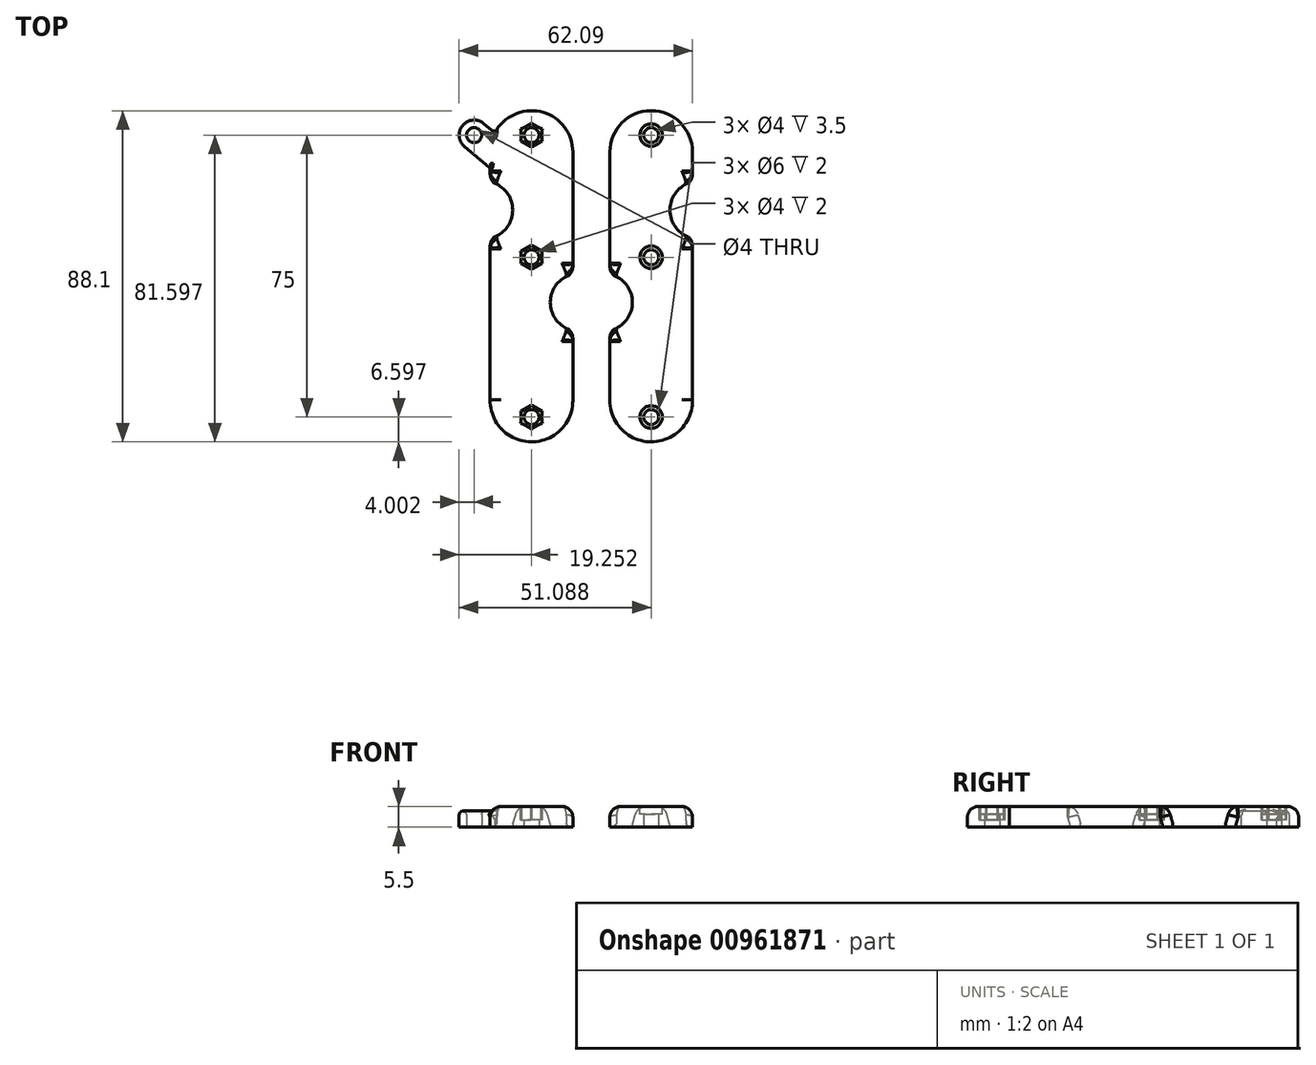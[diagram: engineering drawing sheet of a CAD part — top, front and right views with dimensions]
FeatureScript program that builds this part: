
annotation { "Feature Type Name" : "Feature", "Feature Type Description" : "" }
export const myFeature = defineFeature(function(context is Context, id is Id, definition is map)
    precondition{}
    {
        {
            var Q0;
            Q0=qCreatedBy(makeId("Top.planeOp"),FACE);
            var sketch = newSketch(context, id + "F0", { "sketchPlane" : qUnion([Q0])});
            skCircle(sketch, "E0", {"center": v(-15.92, -0.56) * mm, "radius": 2 * mm});
            skCircle(sketch, "E1", {"center": v(-15.92, 31.94) * mm, "radius": 2 * mm});
            skCircle(sketch, "E2", {"center": v(-15.92, -43.06) * mm, "radius": 2 * mm});
            skLineSegment(sketch, "E3", {"start": v(-26.92, 27.44) * mm, "end": v(-26.92, -38.46) * mm});
            skLineSegment(sketch, "E4", {"start": v(-4.92, 27.44) * mm, "end": v(-4.92, -38.66) * mm});
            skLineSegment(sketch, "E5", {"start": v(-26.92, 27.44) * mm, "end": v(-4.92, 27.44) * mm, "construction": true});
            skPoint(sketch, "E6", {"position": v(-15.92, 27.44) * mm});
            skPoint(sketch, "E7", {"position": v(-17.92, 31.94) * mm});
            skPoint(sketch, "E8", {"position": v(-13.92, 31.94) * mm});
            skLineSegment(sketch, "E9", {"start": v(-26.92, -38.46) * mm, "end": v(-4.92, -38.66) * mm, "construction": true});
            skPoint(sketch, "E10", {"position": v(-15.92, -38.56) * mm});
            skArc(sketch, "E11", {"start": v(-4.92, 27.44) * mm, "mid": v(-15.92, 38.44) * mm, "end": v(-26.92, 27.44) * mm});
            skArc(sketch, "E12", {"start": v(-26.92, -38.46) * mm, "mid": v(-16.02, -49.66) * mm, "end": v(-4.92, -38.66) * mm});
            skPoint(sketch, "E13", {"position": v(-26.92, 12) * mm});
            skPoint(sketch, "E14", {"position": v(-4.92, -12.56) * mm});
            skPoint(sketch, "E15", {"position": v(-26.92, 0) * mm});
            skPoint(sketch, "E16", {"position": v(-4.92, -0.56) * mm});
            skArc(sketch, "E17", {"start": v(-26.92, 4.5) * mm, "mid": v(-20.92, 12) * mm, "end": v(-26.92, 19.5) * mm});
            skArc(sketch, "E18", {"start": v(-4.92, -5.06) * mm, "mid": v(-10.92, -12.56) * mm, "end": v(-4.92, -20.06) * mm});
            skSolve(sketch);
        }
        {
            var Q0;
            Q0=makeQuery(id+"F0.imprint","IMPRINT",FACE,{"disambiguationData":[TD([[makeQuery(id+"F0.imprint","IMPRINT",EDGE,{"derivedFrom":sQuery(id+"F0.wireOp",EDGE,"E0")}),-1.0]])]});
            extrude(context, id + "F1", {"entities" : qUnion([Q0]), "depth" : 5.5 * mm, "offsetDistance" : 25 * mm});
        }
        {
            var Q0;
            Q0=makeQuery(id+"F1.opExtrude","CAP_EDGE",EDGE,{"disambiguationData":[OSD([sQuery(id+"F0.wireOp",EDGE,"E17")])],"isStart":false});
            var Q1;
            Q1=makeQuery(id+"F1.opExtrude","CAP_EDGE",EDGE,{"disambiguationData":[OSD([sQuery(id+"F0.wireOp",EDGE,"E18")])],"isStart":false});
            chamfer(context, id + "F2", {"entities" : qUnion([Q0, Q1]), "chamferType" : ChamferType.OFFSET_ANGLE, "width" : 5 * mm, "oppositeDirection" : false, "angle" : 15 * degree, "tangentPropagation" : true});
        }
        {
            var Q0;
            {var subQ0=sQuery(id+"F0.wireOp",EDGE,"E3");Q0=makeQuery(id+"F1.opExtrude","CAP_EDGE",EDGE,{"disambiguationData":[OSD([subQ0]),TDD([makeQuery(id+"F0.imprint","IMPRINT",EDGE,{"disambiguationData":[TD([[makeQuery(id+"F0.imprint","INTERSECT",VERTEX,{"derivedFrom":[subQ0,sQuery(id+"F0.wireOp",EDGE,"E12")]}),1.0]])],"derivedFrom":subQ0})])],"isStart":false});}
            var Q1;
            Q1=makeQuery(id+"F1.opExtrude","CAP_EDGE",EDGE,{"disambiguationData":[OSD([sQuery(id+"F0.wireOp",EDGE,"E11")])],"isStart":false});
            var Q2;
            Q2=makeQuery(id+"F1.opExtrude","CAP_EDGE",EDGE,{"disambiguationData":[OSD([sQuery(id+"F0.wireOp",EDGE,"E12")])],"isStart":false});
            fillet(context, id + "F3", {"entities" : qUnion([Q0, Q1, Q2]), "radius" : 2.85 * mm, "tangentPropagation" : true, "allowEdgeOverflow" : false});
        }
        {
            var Q0;
            {var subQ0=sQuery(id+"F0.wireOp",EDGE,"E17");Q0=makeQuery(id+"F2.opChamfer","BLEND_EDGE",EDGE,{"blendedFrom":[makeQuery(id+"F1.opExtrude","CAP_EDGE",EDGE,{"disambiguationData":[OSD([subQ0])],"isStart":false}),makeQuery(id+"F1.opExtrude","SWEPT_FACE",FACE,{"disambiguationData":[OSD([subQ0])]})],"blendedInto":[makeQuery(id+"F1.opExtrude","SWEPT_FACE",FACE,{"disambiguationData":[OSD([subQ0])]})]});}
            var Q1;
            {var subQ0=sQuery(id+"F0.wireOp",EDGE,"E18");Q1=makeQuery(id+"F2.opChamfer","BLEND_EDGE",EDGE,{"blendedFrom":[makeQuery(id+"F1.opExtrude","CAP_EDGE",EDGE,{"disambiguationData":[OSD([subQ0])],"isStart":false}),makeQuery(id+"F1.opExtrude","SWEPT_FACE",FACE,{"disambiguationData":[OSD([subQ0])]})],"blendedInto":[makeQuery(id+"F1.opExtrude","SWEPT_FACE",FACE,{"disambiguationData":[OSD([subQ0])]})]});}
            var Q2;
            {var subQ0=sQuery(id+"F0.wireOp",EDGE,"E17");Q2=makeQuery(id+"F2.opChamfer","BLEND_EDGE",EDGE,{"blendedFrom":[makeQuery(id+"F1.opExtrude","CAP_EDGE",EDGE,{"disambiguationData":[OSD([subQ0])],"isStart":false}),makeQuery(id+"F1.opExtrude","CAP_FACE",FACE,{"disambiguationData":[OSD([sQuery(id+"F0.wireOp",EDGE,"E0"),sQuery(id+"F0.wireOp",EDGE,"E1"),sQuery(id+"F0.wireOp",EDGE,"E2"),sQuery(id+"F0.wireOp",EDGE,"E3"),sQuery(id+"F0.wireOp",EDGE,"E4"),sQuery(id+"F0.wireOp",EDGE,"E11"),sQuery(id+"F0.wireOp",EDGE,"E12"),subQ0,sQuery(id+"F0.wireOp",EDGE,"E18")])],"isStart":false})],"blendedInto":[makeQuery(id+"F1.opExtrude","CAP_FACE",FACE,{"disambiguationData":[OSD([sQuery(id+"F0.wireOp",EDGE,"E0"),sQuery(id+"F0.wireOp",EDGE,"E1"),sQuery(id+"F0.wireOp",EDGE,"E2"),sQuery(id+"F0.wireOp",EDGE,"E3"),sQuery(id+"F0.wireOp",EDGE,"E4"),sQuery(id+"F0.wireOp",EDGE,"E11"),sQuery(id+"F0.wireOp",EDGE,"E12"),subQ0,sQuery(id+"F0.wireOp",EDGE,"E18")])],"isStart":false})]});}
            var Q3;
            {var subQ0=sQuery(id+"F0.wireOp",EDGE,"E18");Q3=makeQuery(id+"F2.opChamfer","BLEND_EDGE",EDGE,{"blendedFrom":[makeQuery(id+"F1.opExtrude","CAP_EDGE",EDGE,{"disambiguationData":[OSD([subQ0])],"isStart":false}),makeQuery(id+"F1.opExtrude","CAP_FACE",FACE,{"disambiguationData":[OSD([sQuery(id+"F0.wireOp",EDGE,"E0"),sQuery(id+"F0.wireOp",EDGE,"E1"),sQuery(id+"F0.wireOp",EDGE,"E2"),sQuery(id+"F0.wireOp",EDGE,"E3"),sQuery(id+"F0.wireOp",EDGE,"E4"),sQuery(id+"F0.wireOp",EDGE,"E11"),sQuery(id+"F0.wireOp",EDGE,"E12"),sQuery(id+"F0.wireOp",EDGE,"E17"),subQ0])],"isStart":false})],"blendedInto":[makeQuery(id+"F1.opExtrude","CAP_FACE",FACE,{"disambiguationData":[OSD([sQuery(id+"F0.wireOp",EDGE,"E0"),sQuery(id+"F0.wireOp",EDGE,"E1"),sQuery(id+"F0.wireOp",EDGE,"E2"),sQuery(id+"F0.wireOp",EDGE,"E3"),sQuery(id+"F0.wireOp",EDGE,"E4"),sQuery(id+"F0.wireOp",EDGE,"E11"),sQuery(id+"F0.wireOp",EDGE,"E12"),sQuery(id+"F0.wireOp",EDGE,"E17"),subQ0])],"isStart":false})]});}
            fillet(context, id + "F4", {"entities" : qUnion([Q0, Q1, Q2, Q3]), "radius" : 3 * mm, "tangentPropagation" : true, "allowEdgeOverflow" : false});
        }
        {
            var Q0;
            Q0=makeQuery(id+"F1.opExtrude","SWEPT_BODY",BODY,{"disambiguationData":[OSD([sQuery(id+"F0.wireOp",EDGE,"E0"),sQuery(id+"F0.wireOp",EDGE,"E1"),sQuery(id+"F0.wireOp",EDGE,"E2"),sQuery(id+"F0.wireOp",EDGE,"E3"),sQuery(id+"F0.wireOp",EDGE,"E4"),sQuery(id+"F0.wireOp",EDGE,"E11"),sQuery(id+"F0.wireOp",EDGE,"E12"),sQuery(id+"F0.wireOp",EDGE,"E17"),sQuery(id+"F0.wireOp",EDGE,"E18")])]});
            var Q1;
            Q1=qCreatedBy(makeId("Right.planeOp"),FACE);
            mirror(context, id + "F5", {"entities" : qUnion([Q0]), "mirrorPlane" : qUnion([Q1])});
        }
        {
            var Q0;
            Q0=makeQuery(id+"F5.opPattern","COPY",FACE,{"derivedFrom":makeQuery(id+"F1.opExtrude","CAP_FACE",FACE,{"disambiguationData":[OSD([sQuery(id+"F0.wireOp",EDGE,"E0"),sQuery(id+"F0.wireOp",EDGE,"E1"),sQuery(id+"F0.wireOp",EDGE,"E2"),sQuery(id+"F0.wireOp",EDGE,"E3"),sQuery(id+"F0.wireOp",EDGE,"E4"),sQuery(id+"F0.wireOp",EDGE,"E11"),sQuery(id+"F0.wireOp",EDGE,"E12"),sQuery(id+"F0.wireOp",EDGE,"E17"),sQuery(id+"F0.wireOp",EDGE,"E18")])],"isStart":false}),"instanceName":"1"});
            var sketch = newSketch(context, id + "F6", { "sketchPlane" : qUnion([Q0])});
            skCircle(sketch, "E19", {"center": v(15.92, -0.56) * mm, "radius": 3 * mm});
            skCircle(sketch, "E20", {"center": v(15.92, -43.06) * mm, "radius": 3 * mm});
            skCircle(sketch, "E21", {"center": v(15.92, 31.94) * mm, "radius": 3 * mm});
            skSolve(sketch);
        }
        {
            var Q0;
            Q0=makeQuery(id+"F6.imprint","IMPRINT",FACE,{"disambiguationData":[TD([[makeQuery(id+"F6.imprint","IMPRINT",EDGE,{"derivedFrom":sQuery(id+"F6.wireOp",EDGE,"E21")}),1.0]])]});
            var Q1;
            Q1=makeQuery(id+"F6.imprint","IMPRINT",FACE,{"disambiguationData":[TD([[makeQuery(id+"F6.imprint","IMPRINT",EDGE,{"derivedFrom":sQuery(id+"F6.wireOp",EDGE,"E19")}),1.0]])]});
            var Q2;
            Q2=makeQuery(id+"F6.imprint","IMPRINT",FACE,{"disambiguationData":[TD([[makeQuery(id+"F6.imprint","IMPRINT",EDGE,{"derivedFrom":sQuery(id+"F6.wireOp",EDGE,"E20")}),1.0]])]});
            extrude(context, id + "F7", {"entities" : qUnion([Q0, Q1, Q2]), "operationType" : NewBodyOperationType.REMOVE, "oppositeDirection" : true, "depth" : 2 * mm, "offsetDistance" : 25 * mm});
        }
        {
            var Q0;
            Q0=makeQuery(id+"F1.opExtrude","CAP_FACE",FACE,{"disambiguationData":[OSD([sQuery(id+"F0.wireOp",EDGE,"E0"),sQuery(id+"F0.wireOp",EDGE,"E1"),sQuery(id+"F0.wireOp",EDGE,"E2"),sQuery(id+"F0.wireOp",EDGE,"E3"),sQuery(id+"F0.wireOp",EDGE,"E4"),sQuery(id+"F0.wireOp",EDGE,"E11"),sQuery(id+"F0.wireOp",EDGE,"E12"),sQuery(id+"F0.wireOp",EDGE,"E17"),sQuery(id+"F0.wireOp",EDGE,"E18")])],"isStart":false});
            var sketch = newSketch(context, id + "F8", { "sketchPlane" : qUnion([Q0])});
            skCircle(sketch, "E22.cCircle", {"center": v(-15.92, -0.56) * mm, "radius": 2.75 * mm, "construction": true});
            skLineSegment(sketch, "E22.0", {"start": v(-15.92, 2.61) * mm, "end": v(-13.17, 1.03) * mm});
            skLineSegment(sketch, "E22.1", {"start": v(-13.17, 1.03) * mm, "end": v(-13.17, -2.15) * mm});
            skLineSegment(sketch, "E22.2", {"start": v(-13.17, -2.15) * mm, "end": v(-15.92, -3.74) * mm});
            skLineSegment(sketch, "E22.3", {"start": v(-15.92, -3.74) * mm, "end": v(-18.67, -2.15) * mm});
            skLineSegment(sketch, "E22.4", {"start": v(-18.67, -2.15) * mm, "end": v(-18.67, 1.03) * mm});
            skLineSegment(sketch, "E22.5", {"start": v(-18.67, 1.03) * mm, "end": v(-15.92, 2.61) * mm});
            skPoint(sketch, "E22.0.midPoint", {"position": v(-14.54, 1.82) * mm});
            skCircle(sketch, "E23.cCircle", {"center": v(-15.92, 31.94) * mm, "radius": 2.75 * mm, "construction": true});
            skLineSegment(sketch, "E23.0", {"start": v(-13.17, 30.35) * mm, "end": v(-15.92, 28.76) * mm});
            skLineSegment(sketch, "E23.1", {"start": v(-15.92, 28.76) * mm, "end": v(-18.67, 30.35) * mm});
            skLineSegment(sketch, "E23.2", {"start": v(-18.67, 30.35) * mm, "end": v(-18.67, 33.53) * mm});
            skLineSegment(sketch, "E23.3", {"start": v(-18.67, 33.53) * mm, "end": v(-15.92, 35.11) * mm});
            skLineSegment(sketch, "E23.4", {"start": v(-15.92, 35.11) * mm, "end": v(-13.17, 33.53) * mm});
            skLineSegment(sketch, "E23.5", {"start": v(-13.17, 33.53) * mm, "end": v(-13.17, 30.35) * mm});
            skPoint(sketch, "E23.0.midPoint", {"position": v(-14.54, 29.56) * mm});
            skCircle(sketch, "E24.cCircle", {"center": v(-15.92, -43.06) * mm, "radius": 2.75 * mm, "construction": true});
            skLineSegment(sketch, "E24.0", {"start": v(-15.92, -39.89) * mm, "end": v(-13.17, -41.47) * mm});
            skLineSegment(sketch, "E24.1", {"start": v(-13.17, -41.47) * mm, "end": v(-13.17, -44.65) * mm});
            skLineSegment(sketch, "E24.2", {"start": v(-13.17, -44.65) * mm, "end": v(-15.92, -46.24) * mm});
            skLineSegment(sketch, "E24.3", {"start": v(-15.92, -46.24) * mm, "end": v(-18.67, -44.65) * mm});
            skLineSegment(sketch, "E24.4", {"start": v(-18.67, -44.65) * mm, "end": v(-18.67, -41.47) * mm});
            skLineSegment(sketch, "E24.5", {"start": v(-18.67, -41.47) * mm, "end": v(-15.92, -39.89) * mm});
            skPoint(sketch, "E24.0.midPoint", {"position": v(-14.54, -40.68) * mm});
            skCircle(sketch, "E25.cCircle", {"center": v(-15.92, -0.56) * mm, "radius": 1.69 * mm, "construction": true});
            skLineSegment(sketch, "E25.0", {"start": v(-13, -2.25) * mm, "end": v(-15.92, 2.81) * mm});
            skLineSegment(sketch, "E25.1", {"start": v(-13, -2.25) * mm, "end": v(-18.84, -2.25) * mm});
            skLineSegment(sketch, "E25.2", {"start": v(-15.92, 2.81) * mm, "end": v(-18.84, -2.25) * mm});
            skPoint(sketch, "E25.0.midPoint", {"position": v(-14.46, 0.28) * mm});
            skLineSegment(sketch, "E26.0", {"start": v(-13, 1.13) * mm, "end": v(-15.92, -3.94) * mm});
            skLineSegment(sketch, "E26.1", {"start": v(-15.92, -3.94) * mm, "end": v(-18.84, 1.13) * mm});
            skLineSegment(sketch, "E26.2", {"start": v(-18.84, 1.13) * mm, "end": v(-13, 1.13) * mm});
            skPoint(sketch, "E26.0.midPoint", {"position": v(-14.46, -1.4) * mm});
            skCircle(sketch, "E27.cCircle", {"center": v(-15.92, 31.94) * mm, "radius": 1.69 * mm, "construction": true});
            skLineSegment(sketch, "E27.0", {"start": v(-18.84, 33.63) * mm, "end": v(-13, 33.63) * mm});
            skLineSegment(sketch, "E27.1", {"start": v(-13, 33.63) * mm, "end": v(-15.92, 28.56) * mm});
            skLineSegment(sketch, "E27.2", {"start": v(-15.92, 28.56) * mm, "end": v(-18.84, 33.63) * mm});
            skPoint(sketch, "E27.0.midPoint", {"position": v(-15.92, 33.63) * mm});
            skLineSegment(sketch, "E28.0", {"start": v(-13, 30.25) * mm, "end": v(-18.84, 30.25) * mm});
            skLineSegment(sketch, "E28.1", {"start": v(-18.84, 30.25) * mm, "end": v(-15.92, 35.31) * mm});
            skLineSegment(sketch, "E28.2", {"start": v(-15.92, 35.31) * mm, "end": v(-13, 30.25) * mm});
            skPoint(sketch, "E28.0.midPoint", {"position": v(-15.92, 30.25) * mm});
            skCircle(sketch, "E29.cCircle", {"center": v(-15.92, -43.06) * mm, "radius": 1.69 * mm, "construction": true});
            skLineSegment(sketch, "E29.0", {"start": v(-18.84, -41.37) * mm, "end": v(-13, -41.37) * mm});
            skLineSegment(sketch, "E29.1", {"start": v(-13, -41.37) * mm, "end": v(-15.92, -46.44) * mm});
            skLineSegment(sketch, "E29.2", {"start": v(-15.92, -46.44) * mm, "end": v(-18.84, -41.37) * mm});
            skPoint(sketch, "E29.0.midPoint", {"position": v(-15.92, -41.37) * mm});
            skLineSegment(sketch, "E30.0", {"start": v(-13, -44.75) * mm, "end": v(-18.84, -44.75) * mm});
            skLineSegment(sketch, "E30.1", {"start": v(-18.84, -44.75) * mm, "end": v(-15.92, -39.69) * mm});
            skLineSegment(sketch, "E30.2", {"start": v(-15.92, -39.69) * mm, "end": v(-13, -44.75) * mm});
            skPoint(sketch, "E30.0.midPoint", {"position": v(-15.92, -44.75) * mm});
            skSolve(sketch);
        }
        {
            var Q0;
            {var subQ0=sQuery(id+"F8.wireOp",EDGE,"E22.5");var subQ1=sQuery(id+"F8.wireOp",EDGE,"E22.4");var subQ2=makeQuery(id+"F8.imprint","INTERSECT",VERTEX,{"derivedFrom":[subQ1,subQ0]});Q0=makeQuery(id+"F8.imprint","IMPRINT",FACE,{"disambiguationData":[TD([[makeQuery(id+"F8.imprint","IMPRINT",EDGE,{"disambiguationData":[TD([[subQ2,1.0]])],"derivedFrom":subQ1}),1.0]])]});}
            var Q1;
            {var subQ1=sQuery(id+"F8.wireOp",EDGE,"E22.5");var subQ6=sQuery(id+"F8.wireOp",EDGE,"E22.4");var subQ9=makeQuery(id+"F8.imprint","INTERSECT",VERTEX,{"derivedFrom":[subQ6,subQ1]});Q1=makeQuery(id+"F8.imprint","IMPRINT",FACE,{"disambiguationData":[TD([[makeQuery(id+"F8.imprint","IMPRINT",EDGE,{"disambiguationData":[TD([[subQ9,1.0]])],"derivedFrom":subQ6}),-1.0]])]});}
            var Q2;
            {var subQ0=sQuery(id+"F8.wireOp",EDGE,"E26.2");var subQ1=sQuery(id+"F8.wireOp",EDGE,"E22.5");var subQ2=makeQuery(id+"F8.imprint","INTERSECT",VERTEX,{"derivedFrom":[subQ1,subQ0]});Q2=makeQuery(id+"F8.imprint","IMPRINT",FACE,{"disambiguationData":[TD([[makeQuery(id+"F8.imprint","IMPRINT",EDGE,{"disambiguationData":[TD([[subQ2,-1.0]])],"derivedFrom":subQ1}),-1.0]])]});}
            var Q3;
            {var subQ0=sQuery(id+"F8.wireOp",EDGE,"E25.2");var subQ1=sQuery(id+"F8.wireOp",EDGE,"E22.4");var subQ2=makeQuery(id+"F8.imprint","INTERSECT",VERTEX,{"derivedFrom":[subQ1,subQ0]});Q3=makeQuery(id+"F8.imprint","IMPRINT",FACE,{"disambiguationData":[TD([[makeQuery(id+"F8.imprint","IMPRINT",EDGE,{"disambiguationData":[TD([[subQ2,-1.0]])],"derivedFrom":subQ1}),-1.0]])]});}
            var Q4;
            {var subQ0=sQuery(id+"F8.wireOp",EDGE,"E22.4");var subQ1=sQuery(id+"F8.wireOp",EDGE,"E22.3");var subQ2=makeQuery(id+"F8.imprint","INTERSECT",VERTEX,{"derivedFrom":[subQ1,subQ0]});Q4=makeQuery(id+"F8.imprint","IMPRINT",FACE,{"disambiguationData":[TD([[makeQuery(id+"F8.imprint","IMPRINT",EDGE,{"disambiguationData":[TD([[subQ2,1.0]])],"derivedFrom":subQ1}),1.0]])]});}
            var Q5;
            {var subQ1=sQuery(id+"F8.wireOp",EDGE,"E22.4");var subQ6=sQuery(id+"F8.wireOp",EDGE,"E22.3");var subQ9=makeQuery(id+"F8.imprint","INTERSECT",VERTEX,{"derivedFrom":[subQ6,subQ1]});Q5=makeQuery(id+"F8.imprint","IMPRINT",FACE,{"disambiguationData":[TD([[makeQuery(id+"F8.imprint","IMPRINT",EDGE,{"disambiguationData":[TD([[subQ9,1.0]])],"derivedFrom":subQ6}),-1.0]])]});}
            var Q6;
            {var subQ0=sQuery(id+"F8.wireOp",EDGE,"E26.1");var subQ1=sQuery(id+"F8.wireOp",EDGE,"E22.3");var subQ2=makeQuery(id+"F8.imprint","INTERSECT",VERTEX,{"derivedFrom":[subQ1,subQ0]});Q6=makeQuery(id+"F8.imprint","IMPRINT",FACE,{"disambiguationData":[TD([[makeQuery(id+"F8.imprint","IMPRINT",EDGE,{"disambiguationData":[TD([[subQ2,-1.0]])],"derivedFrom":subQ1}),-1.0]])]});}
            var Q7;
            {var subQ1=sQuery(id+"F8.wireOp",EDGE,"E22.2");var subQ6=sQuery(id+"F8.wireOp",EDGE,"E22.3");var subQ9=makeQuery(id+"F8.imprint","INTERSECT",VERTEX,{"derivedFrom":[subQ1,subQ6]});Q7=makeQuery(id+"F8.imprint","IMPRINT",FACE,{"disambiguationData":[TD([[makeQuery(id+"F8.imprint","IMPRINT",EDGE,{"disambiguationData":[TD([[subQ9,1.0]])],"derivedFrom":subQ1}),-1.0]])]});}
            var Q8;
            {var subQ0=sQuery(id+"F8.wireOp",EDGE,"E25.1");var subQ1=sQuery(id+"F8.wireOp",EDGE,"E22.2");var subQ2=makeQuery(id+"F8.imprint","INTERSECT",VERTEX,{"derivedFrom":[subQ1,subQ0]});Q8=makeQuery(id+"F8.imprint","IMPRINT",FACE,{"disambiguationData":[TD([[makeQuery(id+"F8.imprint","IMPRINT",EDGE,{"disambiguationData":[TD([[subQ2,-1.0]])],"derivedFrom":subQ1}),-1.0]])]});}
            var Q9;
            {var subQ1=sQuery(id+"F8.wireOp",EDGE,"E22.2");var subQ5=sQuery(id+"F8.wireOp",EDGE,"E22.1");var subQ6=makeQuery(id+"F8.imprint","INTERSECT",VERTEX,{"derivedFrom":[subQ5,subQ1]});Q9=makeQuery(id+"F8.imprint","IMPRINT",FACE,{"disambiguationData":[TD([[makeQuery(id+"F8.imprint","IMPRINT",EDGE,{"disambiguationData":[TD([[subQ6,1.0]])],"derivedFrom":subQ5}),-1.0]])]});}
            var Q10;
            {var subQ0=sQuery(id+"F8.wireOp",EDGE,"E26.0");var subQ1=sQuery(id+"F8.wireOp",EDGE,"E22.1");var subQ2=makeQuery(id+"F8.imprint","INTERSECT",VERTEX,{"derivedFrom":[subQ1,subQ0]});Q10=makeQuery(id+"F8.imprint","IMPRINT",FACE,{"disambiguationData":[TD([[makeQuery(id+"F8.imprint","IMPRINT",EDGE,{"disambiguationData":[TD([[subQ2,-1.0]])],"derivedFrom":subQ1}),-1.0]])]});}
            var Q11;
            {var subQ1=sQuery(id+"F8.wireOp",EDGE,"E22.0");var subQ5=sQuery(id+"F8.wireOp",EDGE,"E22.1");var subQ6=makeQuery(id+"F8.imprint","INTERSECT",VERTEX,{"derivedFrom":[subQ1,subQ5]});Q11=makeQuery(id+"F8.imprint","IMPRINT",FACE,{"disambiguationData":[TD([[makeQuery(id+"F8.imprint","IMPRINT",EDGE,{"disambiguationData":[TD([[subQ6,1.0]])],"derivedFrom":subQ1}),-1.0]])]});}
            var Q12;
            {var subQ0=sQuery(id+"F8.wireOp",EDGE,"E25.0");var subQ1=sQuery(id+"F8.wireOp",EDGE,"E22.0");var subQ2=makeQuery(id+"F8.imprint","INTERSECT",VERTEX,{"derivedFrom":[subQ1,subQ0]});Q12=makeQuery(id+"F8.imprint","IMPRINT",FACE,{"disambiguationData":[TD([[makeQuery(id+"F8.imprint","IMPRINT",EDGE,{"disambiguationData":[TD([[subQ2,-1.0]])],"derivedFrom":subQ1}),-1.0]])]});}
            var Q13;
            {var subQ0=sQuery(id+"F8.wireOp",EDGE,"E22.5");var subQ1=sQuery(id+"F8.wireOp",EDGE,"E22.0");var subQ2=makeQuery(id+"F8.imprint","INTERSECT",VERTEX,{"derivedFrom":[subQ1,subQ0]});Q13=makeQuery(id+"F8.imprint","IMPRINT",FACE,{"disambiguationData":[TD([[makeQuery(id+"F8.imprint","IMPRINT",EDGE,{"disambiguationData":[TD([[subQ2,-1.0]])],"derivedFrom":subQ1}),-1.0]])]});}
            var Q14;
            {var subQ0=sQuery(id+"F8.wireOp",EDGE,"E22.3");var subQ1=sQuery(id+"F8.wireOp",EDGE,"E22.2");var subQ2=makeQuery(id+"F8.imprint","INTERSECT",VERTEX,{"derivedFrom":[subQ1,subQ0]});Q14=makeQuery(id+"F8.imprint","IMPRINT",FACE,{"disambiguationData":[TD([[makeQuery(id+"F8.imprint","IMPRINT",EDGE,{"disambiguationData":[TD([[subQ2,1.0]])],"derivedFrom":subQ1}),1.0]])]});}
            var Q15;
            {var subQ0=sQuery(id+"F8.wireOp",EDGE,"E22.2");var subQ1=sQuery(id+"F8.wireOp",EDGE,"E22.1");var subQ2=makeQuery(id+"F8.imprint","INTERSECT",VERTEX,{"derivedFrom":[subQ1,subQ0]});Q15=makeQuery(id+"F8.imprint","IMPRINT",FACE,{"disambiguationData":[TD([[makeQuery(id+"F8.imprint","IMPRINT",EDGE,{"disambiguationData":[TD([[subQ2,1.0]])],"derivedFrom":subQ1}),1.0]])]});}
            var Q16;
            {var subQ0=sQuery(id+"F8.wireOp",EDGE,"E22.1");var subQ1=sQuery(id+"F8.wireOp",EDGE,"E22.0");var subQ2=makeQuery(id+"F8.imprint","INTERSECT",VERTEX,{"derivedFrom":[subQ1,subQ0]});Q16=makeQuery(id+"F8.imprint","IMPRINT",FACE,{"disambiguationData":[TD([[makeQuery(id+"F8.imprint","IMPRINT",EDGE,{"disambiguationData":[TD([[subQ2,1.0]])],"derivedFrom":subQ1}),1.0]])]});}
            var Q17;
            {var subQ0=sQuery(id+"F8.wireOp",EDGE,"E22.5");var subQ1=sQuery(id+"F8.wireOp",EDGE,"E22.0");var subQ2=makeQuery(id+"F8.imprint","INTERSECT",VERTEX,{"derivedFrom":[subQ1,subQ0]});Q17=makeQuery(id+"F8.imprint","IMPRINT",FACE,{"disambiguationData":[TD([[makeQuery(id+"F8.imprint","IMPRINT",EDGE,{"disambiguationData":[TD([[subQ2,-1.0]])],"derivedFrom":subQ1}),1.0]])]});}
            var Q18;
            {var subQ0=sQuery(id+"F8.wireOp",EDGE,"E27.2");var subQ1=sQuery(id+"F8.wireOp",EDGE,"E23.1");var subQ2=makeQuery(id+"F8.imprint","INTERSECT",VERTEX,{"derivedFrom":[subQ1,subQ0]});Q18=makeQuery(id+"F8.imprint","IMPRINT",FACE,{"disambiguationData":[TD([[makeQuery(id+"F8.imprint","IMPRINT",EDGE,{"disambiguationData":[TD([[subQ2,-1.0]])],"derivedFrom":subQ1}),-1.0]])]});}
            var Q19;
            {var subQ1=sQuery(id+"F8.wireOp",EDGE,"E23.1");var subQ6=sQuery(id+"F8.wireOp",EDGE,"E23.0");var subQ9=makeQuery(id+"F8.imprint","INTERSECT",VERTEX,{"derivedFrom":[subQ6,subQ1]});Q19=makeQuery(id+"F8.imprint","IMPRINT",FACE,{"disambiguationData":[TD([[makeQuery(id+"F8.imprint","IMPRINT",EDGE,{"disambiguationData":[TD([[subQ9,1.0]])],"derivedFrom":subQ6}),-1.0]])]});}
            var Q20;
            {var subQ0=sQuery(id+"F8.wireOp",EDGE,"E28.0");var subQ1=sQuery(id+"F8.wireOp",EDGE,"E23.0");var subQ2=makeQuery(id+"F8.imprint","INTERSECT",VERTEX,{"derivedFrom":[subQ1,subQ0]});Q20=makeQuery(id+"F8.imprint","IMPRINT",FACE,{"disambiguationData":[TD([[makeQuery(id+"F8.imprint","IMPRINT",EDGE,{"disambiguationData":[TD([[subQ2,-1.0]])],"derivedFrom":subQ1}),-1.0]])]});}
            var Q21;
            {var subQ1=sQuery(id+"F8.wireOp",EDGE,"E23.5");var subQ6=sQuery(id+"F8.wireOp",EDGE,"E23.0");var subQ9=makeQuery(id+"F8.imprint","INTERSECT",VERTEX,{"derivedFrom":[subQ6,subQ1]});Q21=makeQuery(id+"F8.imprint","IMPRINT",FACE,{"disambiguationData":[TD([[makeQuery(id+"F8.imprint","IMPRINT",EDGE,{"disambiguationData":[TD([[subQ9,-1.0]])],"derivedFrom":subQ6}),-1.0]])]});}
            var Q22;
            {var subQ0=sQuery(id+"F8.wireOp",EDGE,"E27.1");var subQ1=sQuery(id+"F8.wireOp",EDGE,"E23.5");var subQ2=makeQuery(id+"F8.imprint","INTERSECT",VERTEX,{"derivedFrom":[subQ1,subQ0]});Q22=makeQuery(id+"F8.imprint","IMPRINT",FACE,{"disambiguationData":[TD([[makeQuery(id+"F8.imprint","IMPRINT",EDGE,{"disambiguationData":[TD([[subQ2,-1.0]])],"derivedFrom":subQ1}),-1.0]])]});}
            var Q23;
            {var subQ1=sQuery(id+"F8.wireOp",EDGE,"E23.4");var subQ5=sQuery(id+"F8.wireOp",EDGE,"E23.5");var subQ6=makeQuery(id+"F8.imprint","INTERSECT",VERTEX,{"derivedFrom":[subQ1,subQ5]});Q23=makeQuery(id+"F8.imprint","IMPRINT",FACE,{"disambiguationData":[TD([[makeQuery(id+"F8.imprint","IMPRINT",EDGE,{"disambiguationData":[TD([[subQ6,1.0]])],"derivedFrom":subQ1}),-1.0]])]});}
            var Q24;
            {var subQ0=sQuery(id+"F8.wireOp",EDGE,"E28.2");var subQ1=sQuery(id+"F8.wireOp",EDGE,"E23.4");var subQ2=makeQuery(id+"F8.imprint","INTERSECT",VERTEX,{"derivedFrom":[subQ1,subQ0]});Q24=makeQuery(id+"F8.imprint","IMPRINT",FACE,{"disambiguationData":[TD([[makeQuery(id+"F8.imprint","IMPRINT",EDGE,{"disambiguationData":[TD([[subQ2,-1.0]])],"derivedFrom":subQ1}),-1.0]])]});}
            var Q25;
            {var subQ1=sQuery(id+"F8.wireOp",EDGE,"E23.3");var subQ5=sQuery(id+"F8.wireOp",EDGE,"E23.4");var subQ6=makeQuery(id+"F8.imprint","INTERSECT",VERTEX,{"derivedFrom":[subQ1,subQ5]});Q25=makeQuery(id+"F8.imprint","IMPRINT",FACE,{"disambiguationData":[TD([[makeQuery(id+"F8.imprint","IMPRINT",EDGE,{"disambiguationData":[TD([[subQ6,1.0]])],"derivedFrom":subQ1}),-1.0]])]});}
            var Q26;
            {var subQ0=sQuery(id+"F8.wireOp",EDGE,"E27.0");var subQ1=sQuery(id+"F8.wireOp",EDGE,"E23.3");var subQ2=makeQuery(id+"F8.imprint","INTERSECT",VERTEX,{"derivedFrom":[subQ1,subQ0]});Q26=makeQuery(id+"F8.imprint","IMPRINT",FACE,{"disambiguationData":[TD([[makeQuery(id+"F8.imprint","IMPRINT",EDGE,{"disambiguationData":[TD([[subQ2,-1.0]])],"derivedFrom":subQ1}),-1.0]])]});}
            var Q27;
            {var subQ1=sQuery(id+"F8.wireOp",EDGE,"E23.2");var subQ5=sQuery(id+"F8.wireOp",EDGE,"E23.3");var subQ6=makeQuery(id+"F8.imprint","INTERSECT",VERTEX,{"derivedFrom":[subQ1,subQ5]});Q27=makeQuery(id+"F8.imprint","IMPRINT",FACE,{"disambiguationData":[TD([[makeQuery(id+"F8.imprint","IMPRINT",EDGE,{"disambiguationData":[TD([[subQ6,1.0]])],"derivedFrom":subQ1}),-1.0]])]});}
            var Q28;
            {var subQ0=sQuery(id+"F8.wireOp",EDGE,"E28.1");var subQ1=sQuery(id+"F8.wireOp",EDGE,"E23.2");var subQ2=makeQuery(id+"F8.imprint","INTERSECT",VERTEX,{"derivedFrom":[subQ1,subQ0]});Q28=makeQuery(id+"F8.imprint","IMPRINT",FACE,{"disambiguationData":[TD([[makeQuery(id+"F8.imprint","IMPRINT",EDGE,{"disambiguationData":[TD([[subQ2,-1.0]])],"derivedFrom":subQ1}),-1.0]])]});}
            var Q29;
            {var subQ1=sQuery(id+"F8.wireOp",EDGE,"E23.1");var subQ5=sQuery(id+"F8.wireOp",EDGE,"E23.2");var subQ6=makeQuery(id+"F8.imprint","INTERSECT",VERTEX,{"derivedFrom":[subQ1,subQ5]});Q29=makeQuery(id+"F8.imprint","IMPRINT",FACE,{"disambiguationData":[TD([[makeQuery(id+"F8.imprint","IMPRINT",EDGE,{"disambiguationData":[TD([[subQ6,1.0]])],"derivedFrom":subQ1}),-1.0]])]});}
            var Q30;
            {var subQ0=sQuery(id+"F8.wireOp",EDGE,"E23.2");var subQ1=sQuery(id+"F8.wireOp",EDGE,"E23.1");var subQ2=makeQuery(id+"F8.imprint","INTERSECT",VERTEX,{"derivedFrom":[subQ1,subQ0]});Q30=makeQuery(id+"F8.imprint","IMPRINT",FACE,{"disambiguationData":[TD([[makeQuery(id+"F8.imprint","IMPRINT",EDGE,{"disambiguationData":[TD([[subQ2,1.0]])],"derivedFrom":subQ1}),1.0]])]});}
            var Q31;
            {var subQ0=sQuery(id+"F8.wireOp",EDGE,"E23.1");var subQ1=sQuery(id+"F8.wireOp",EDGE,"E23.0");var subQ2=makeQuery(id+"F8.imprint","INTERSECT",VERTEX,{"derivedFrom":[subQ1,subQ0]});Q31=makeQuery(id+"F8.imprint","IMPRINT",FACE,{"disambiguationData":[TD([[makeQuery(id+"F8.imprint","IMPRINT",EDGE,{"disambiguationData":[TD([[subQ2,1.0]])],"derivedFrom":subQ1}),1.0]])]});}
            var Q32;
            {var subQ0=sQuery(id+"F8.wireOp",EDGE,"E23.5");var subQ1=sQuery(id+"F8.wireOp",EDGE,"E23.0");var subQ2=makeQuery(id+"F8.imprint","INTERSECT",VERTEX,{"derivedFrom":[subQ1,subQ0]});Q32=makeQuery(id+"F8.imprint","IMPRINT",FACE,{"disambiguationData":[TD([[makeQuery(id+"F8.imprint","IMPRINT",EDGE,{"disambiguationData":[TD([[subQ2,-1.0]])],"derivedFrom":subQ1}),1.0]])]});}
            var Q33;
            {var subQ0=sQuery(id+"F8.wireOp",EDGE,"E23.4");var subQ1=sQuery(id+"F8.wireOp",EDGE,"E23.3");var subQ2=makeQuery(id+"F8.imprint","INTERSECT",VERTEX,{"derivedFrom":[subQ1,subQ0]});Q33=makeQuery(id+"F8.imprint","IMPRINT",FACE,{"disambiguationData":[TD([[makeQuery(id+"F8.imprint","IMPRINT",EDGE,{"disambiguationData":[TD([[subQ2,1.0]])],"derivedFrom":subQ1}),1.0]])]});}
            var Q34;
            {var subQ0=sQuery(id+"F8.wireOp",EDGE,"E23.5");var subQ1=sQuery(id+"F8.wireOp",EDGE,"E23.4");var subQ2=makeQuery(id+"F8.imprint","INTERSECT",VERTEX,{"derivedFrom":[subQ1,subQ0]});Q34=makeQuery(id+"F8.imprint","IMPRINT",FACE,{"disambiguationData":[TD([[makeQuery(id+"F8.imprint","IMPRINT",EDGE,{"disambiguationData":[TD([[subQ2,1.0]])],"derivedFrom":subQ1}),1.0]])]});}
            var Q35;
            {var subQ0=sQuery(id+"F8.wireOp",EDGE,"E23.3");var subQ1=sQuery(id+"F8.wireOp",EDGE,"E23.2");var subQ2=makeQuery(id+"F8.imprint","INTERSECT",VERTEX,{"derivedFrom":[subQ1,subQ0]});Q35=makeQuery(id+"F8.imprint","IMPRINT",FACE,{"disambiguationData":[TD([[makeQuery(id+"F8.imprint","IMPRINT",EDGE,{"disambiguationData":[TD([[subQ2,1.0]])],"derivedFrom":subQ1}),1.0]])]});}
            var Q36;
            {var subQ0=sQuery(id+"F8.wireOp",EDGE,"E30.1");var subQ1=sQuery(id+"F8.wireOp",EDGE,"E24.4");var subQ2=makeQuery(id+"F8.imprint","INTERSECT",VERTEX,{"derivedFrom":[subQ1,subQ0]});Q36=makeQuery(id+"F8.imprint","IMPRINT",FACE,{"disambiguationData":[TD([[makeQuery(id+"F8.imprint","IMPRINT",EDGE,{"disambiguationData":[TD([[subQ2,-1.0]])],"derivedFrom":subQ1}),-1.0]])]});}
            var Q37;
            {var subQ1=sQuery(id+"F8.wireOp",EDGE,"E24.4");var subQ7=sQuery(id+"F8.wireOp",EDGE,"E24.5");var subQ9=makeQuery(id+"F8.imprint","INTERSECT",VERTEX,{"derivedFrom":[subQ1,subQ7]});Q37=makeQuery(id+"F8.imprint","IMPRINT",FACE,{"disambiguationData":[TD([[makeQuery(id+"F8.imprint","IMPRINT",EDGE,{"disambiguationData":[TD([[subQ9,1.0]])],"derivedFrom":subQ1}),-1.0]])]});}
            var Q38;
            {var subQ0=sQuery(id+"F8.wireOp",EDGE,"E29.0");var subQ1=sQuery(id+"F8.wireOp",EDGE,"E24.5");var subQ2=makeQuery(id+"F8.imprint","INTERSECT",VERTEX,{"derivedFrom":[subQ1,subQ0]});Q38=makeQuery(id+"F8.imprint","IMPRINT",FACE,{"disambiguationData":[TD([[makeQuery(id+"F8.imprint","IMPRINT",EDGE,{"disambiguationData":[TD([[subQ2,-1.0]])],"derivedFrom":subQ1}),-1.0]])]});}
            var Q39;
            {var subQ1=sQuery(id+"F8.wireOp",EDGE,"E24.0");var subQ5=sQuery(id+"F8.wireOp",EDGE,"E24.5");var subQ6=makeQuery(id+"F8.imprint","INTERSECT",VERTEX,{"derivedFrom":[subQ1,subQ5]});Q39=makeQuery(id+"F8.imprint","IMPRINT",FACE,{"disambiguationData":[TD([[makeQuery(id+"F8.imprint","IMPRINT",EDGE,{"disambiguationData":[TD([[subQ6,-1.0]])],"derivedFrom":subQ1}),-1.0]])]});}
            var Q40;
            {var subQ0=sQuery(id+"F8.wireOp",EDGE,"E30.2");var subQ1=sQuery(id+"F8.wireOp",EDGE,"E24.0");var subQ2=makeQuery(id+"F8.imprint","INTERSECT",VERTEX,{"derivedFrom":[subQ1,subQ0]});Q40=makeQuery(id+"F8.imprint","IMPRINT",FACE,{"disambiguationData":[TD([[makeQuery(id+"F8.imprint","IMPRINT",EDGE,{"disambiguationData":[TD([[subQ2,-1.0]])],"derivedFrom":subQ1}),-1.0]])]});}
            var Q41;
            {var subQ1=sQuery(id+"F8.wireOp",EDGE,"E24.1");var subQ5=sQuery(id+"F8.wireOp",EDGE,"E24.0");var subQ6=makeQuery(id+"F8.imprint","INTERSECT",VERTEX,{"derivedFrom":[subQ5,subQ1]});Q41=makeQuery(id+"F8.imprint","IMPRINT",FACE,{"disambiguationData":[TD([[makeQuery(id+"F8.imprint","IMPRINT",EDGE,{"disambiguationData":[TD([[subQ6,1.0]])],"derivedFrom":subQ5}),-1.0]])]});}
            var Q42;
            {var subQ0=sQuery(id+"F8.wireOp",EDGE,"E29.1");var subQ1=sQuery(id+"F8.wireOp",EDGE,"E24.1");var subQ2=makeQuery(id+"F8.imprint","INTERSECT",VERTEX,{"derivedFrom":[subQ1,subQ0]});Q42=makeQuery(id+"F8.imprint","IMPRINT",FACE,{"disambiguationData":[TD([[makeQuery(id+"F8.imprint","IMPRINT",EDGE,{"disambiguationData":[TD([[subQ2,-1.0]])],"derivedFrom":subQ1}),-1.0]])]});}
            var Q43;
            {var subQ1=sQuery(id+"F8.wireOp",EDGE,"E24.1");var subQ6=sQuery(id+"F8.wireOp",EDGE,"E24.2");var subQ9=makeQuery(id+"F8.imprint","INTERSECT",VERTEX,{"derivedFrom":[subQ1,subQ6]});Q43=makeQuery(id+"F8.imprint","IMPRINT",FACE,{"disambiguationData":[TD([[makeQuery(id+"F8.imprint","IMPRINT",EDGE,{"disambiguationData":[TD([[subQ9,1.0]])],"derivedFrom":subQ1}),-1.0]])]});}
            var Q44;
            {var subQ0=sQuery(id+"F8.wireOp",EDGE,"E30.0");var subQ1=sQuery(id+"F8.wireOp",EDGE,"E24.2");var subQ2=makeQuery(id+"F8.imprint","INTERSECT",VERTEX,{"derivedFrom":[subQ1,subQ0]});Q44=makeQuery(id+"F8.imprint","IMPRINT",FACE,{"disambiguationData":[TD([[makeQuery(id+"F8.imprint","IMPRINT",EDGE,{"disambiguationData":[TD([[subQ2,-1.0]])],"derivedFrom":subQ1}),-1.0]])]});}
            var Q45;
            {var subQ1=sQuery(id+"F8.wireOp",EDGE,"E24.3");var subQ6=sQuery(id+"F8.wireOp",EDGE,"E24.2");var subQ9=makeQuery(id+"F8.imprint","INTERSECT",VERTEX,{"derivedFrom":[subQ6,subQ1]});Q45=makeQuery(id+"F8.imprint","IMPRINT",FACE,{"disambiguationData":[TD([[makeQuery(id+"F8.imprint","IMPRINT",EDGE,{"disambiguationData":[TD([[subQ9,1.0]])],"derivedFrom":subQ6}),-1.0]])]});}
            var Q46;
            {var subQ0=sQuery(id+"F8.wireOp",EDGE,"E29.2");var subQ1=sQuery(id+"F8.wireOp",EDGE,"E24.3");var subQ2=makeQuery(id+"F8.imprint","INTERSECT",VERTEX,{"derivedFrom":[subQ1,subQ0]});Q46=makeQuery(id+"F8.imprint","IMPRINT",FACE,{"disambiguationData":[TD([[makeQuery(id+"F8.imprint","IMPRINT",EDGE,{"disambiguationData":[TD([[subQ2,-1.0]])],"derivedFrom":subQ1}),-1.0]])]});}
            var Q47;
            {var subQ1=sQuery(id+"F8.wireOp",EDGE,"E24.3");var subQ5=sQuery(id+"F8.wireOp",EDGE,"E24.4");var subQ6=makeQuery(id+"F8.imprint","INTERSECT",VERTEX,{"derivedFrom":[subQ1,subQ5]});Q47=makeQuery(id+"F8.imprint","IMPRINT",FACE,{"disambiguationData":[TD([[makeQuery(id+"F8.imprint","IMPRINT",EDGE,{"disambiguationData":[TD([[subQ6,1.0]])],"derivedFrom":subQ1}),-1.0]])]});}
            var Q48;
            {var subQ0=sQuery(id+"F8.wireOp",EDGE,"E24.4");var subQ1=sQuery(id+"F8.wireOp",EDGE,"E24.3");var subQ2=makeQuery(id+"F8.imprint","INTERSECT",VERTEX,{"derivedFrom":[subQ1,subQ0]});Q48=makeQuery(id+"F8.imprint","IMPRINT",FACE,{"disambiguationData":[TD([[makeQuery(id+"F8.imprint","IMPRINT",EDGE,{"disambiguationData":[TD([[subQ2,1.0]])],"derivedFrom":subQ1}),1.0]])]});}
            var Q49;
            {var subQ0=sQuery(id+"F8.wireOp",EDGE,"E24.3");var subQ1=sQuery(id+"F8.wireOp",EDGE,"E24.2");var subQ2=makeQuery(id+"F8.imprint","INTERSECT",VERTEX,{"derivedFrom":[subQ1,subQ0]});Q49=makeQuery(id+"F8.imprint","IMPRINT",FACE,{"disambiguationData":[TD([[makeQuery(id+"F8.imprint","IMPRINT",EDGE,{"disambiguationData":[TD([[subQ2,1.0]])],"derivedFrom":subQ1}),1.0]])]});}
            var Q50;
            {var subQ0=sQuery(id+"F8.wireOp",EDGE,"E24.1");var subQ1=sQuery(id+"F8.wireOp",EDGE,"E24.0");var subQ2=makeQuery(id+"F8.imprint","INTERSECT",VERTEX,{"derivedFrom":[subQ1,subQ0]});Q50=makeQuery(id+"F8.imprint","IMPRINT",FACE,{"disambiguationData":[TD([[makeQuery(id+"F8.imprint","IMPRINT",EDGE,{"disambiguationData":[TD([[subQ2,1.0]])],"derivedFrom":subQ1}),1.0]])]});}
            var Q51;
            {var subQ0=sQuery(id+"F8.wireOp",EDGE,"E24.2");var subQ1=sQuery(id+"F8.wireOp",EDGE,"E24.1");var subQ2=makeQuery(id+"F8.imprint","INTERSECT",VERTEX,{"derivedFrom":[subQ1,subQ0]});Q51=makeQuery(id+"F8.imprint","IMPRINT",FACE,{"disambiguationData":[TD([[makeQuery(id+"F8.imprint","IMPRINT",EDGE,{"disambiguationData":[TD([[subQ2,1.0]])],"derivedFrom":subQ1}),1.0]])]});}
            var Q52;
            {var subQ0=sQuery(id+"F8.wireOp",EDGE,"E24.5");var subQ1=sQuery(id+"F8.wireOp",EDGE,"E24.4");var subQ2=makeQuery(id+"F8.imprint","INTERSECT",VERTEX,{"derivedFrom":[subQ1,subQ0]});Q52=makeQuery(id+"F8.imprint","IMPRINT",FACE,{"disambiguationData":[TD([[makeQuery(id+"F8.imprint","IMPRINT",EDGE,{"disambiguationData":[TD([[subQ2,1.0]])],"derivedFrom":subQ1}),1.0]])]});}
            var Q53;
            {var subQ0=sQuery(id+"F8.wireOp",EDGE,"E24.5");var subQ1=sQuery(id+"F8.wireOp",EDGE,"E24.0");var subQ2=makeQuery(id+"F8.imprint","INTERSECT",VERTEX,{"derivedFrom":[subQ1,subQ0]});Q53=makeQuery(id+"F8.imprint","IMPRINT",FACE,{"disambiguationData":[TD([[makeQuery(id+"F8.imprint","IMPRINT",EDGE,{"disambiguationData":[TD([[subQ2,-1.0]])],"derivedFrom":subQ1}),1.0]])]});}
            extrude(context, id + "F9", {"entities" : qUnion([Q0, Q1, Q2, Q3, Q4, Q5, Q6, Q7, Q8, Q9, Q10, Q11, Q12, Q13, Q14, Q15, Q16, Q17, Q18, Q19, Q20, Q21, Q22, Q23, Q24, Q25, Q26, Q27, Q28, Q29, Q30, Q31, Q32, Q33, Q34, Q35, Q36, Q37, Q38, Q39, Q40, Q41, Q42, Q43, Q44, Q45, Q46, Q47, Q48, Q49, Q50, Q51, Q52, Q53]), "operationType" : NewBodyOperationType.REMOVE, "oppositeDirection" : true, "depth" : 3.5 * mm, "offsetDistance" : 25 * mm});
        }
        {
            var Q0;
            Q0=makeQuery(id+"F1.opExtrude","CAP_FACE",FACE,{"disambiguationData":[OSD([sQuery(id+"F0.wireOp",EDGE,"E0"),sQuery(id+"F0.wireOp",EDGE,"E1"),sQuery(id+"F0.wireOp",EDGE,"E2"),sQuery(id+"F0.wireOp",EDGE,"E3"),sQuery(id+"F0.wireOp",EDGE,"E4"),sQuery(id+"F0.wireOp",EDGE,"E11"),sQuery(id+"F0.wireOp",EDGE,"E12"),sQuery(id+"F0.wireOp",EDGE,"E17"),sQuery(id+"F0.wireOp",EDGE,"E18")])],"isStart":true});
            var sketch = newSketch(context, id + "F10", { "sketchPlane" : qUnion([Q0])});
            skCircle(sketch, "E31", {"center": v(-31.17, -31.94) * mm, "radius": 2 * mm});
            skPoint(sketch, "E32", {"position": v(-15.92, -31.94) * mm});
            skCircle(sketch, "E33", {"center": v(-31.17, -31.94) * mm, "radius": 4 * mm});
            skLineSegment(sketch, "E34", {"start": v(-26.92, -23.1) * mm, "end": v(-33.75, -28.88) * mm});
            skLineSegment(sketch, "E35", {"start": v(-28.58, -35) * mm, "end": v(-25.67, -32.53) * mm});
            skLineSegment(sketch, "E36", {"start": v(-25.67, -32.53) * mm, "end": v(-24.87, -31.85) * mm});
            skLineSegment(sketch, "E37", {"start": v(-26.92, -23.1) * mm, "end": v(-24.87, -21.37) * mm});
            skLineSegment(sketch, "E38", {"start": v(-24.87, -31.85) * mm, "end": v(-24.87, -21.37) * mm});
            skSolve(sketch);
        }
        {
            var Q0;
            {var subQ5=sQuery(id+"F10.wireOp",EDGE,"E34");Q0=makeQuery(id+"F10.imprint","IMPRINT",FACE,{"disambiguationData":[TD([[makeQuery(id+"F10.imprint","IMPRINT",EDGE,{"derivedFrom":subQ5}),1.0]])]});}
            var Q1;
            Q1=makeQuery(id+"F10.imprint","IMPRINT",FACE,{"disambiguationData":[TD([[makeQuery(id+"F10.imprint","IMPRINT",EDGE,{"derivedFrom":sQuery(id+"F10.wireOp",EDGE,"E31")}),-1.0]])]});
            var Q2;
            {var subQ6=sQuery(id+"F10.wireOp",EDGE,"E36");Q2=makeQuery(id+"F10.imprint","IMPRINT",FACE,{"disambiguationData":[TD([[makeQuery(id+"F10.imprint","IMPRINT",EDGE,{"derivedFrom":subQ6}),1.0]])]});}
            extrude(context, id + "F11", {"entities" : qUnion([Q0, Q1, Q2]), "operationType" : NewBodyOperationType.ADD, "depth" : -4.3 * mm, "offsetDistance" : 25 * mm});
        }
        {
            var Q0;
            Q0=makeQuery(id+"F11.opExtrude","CAP_EDGE",EDGE,{"disambiguationData":[OSD([sQuery(id+"F10.wireOp",EDGE,"E35"),sQuery(id+"F10.wireOp",EDGE,"E36")])],"isStart":false});
            var Q1;
            Q1=makeQuery(id+"F11.opExtrude","CAP_EDGE",EDGE,{"disambiguationData":[OSD([sQuery(id+"F10.wireOp",EDGE,"E31")])],"isStart":false});
            var Q2;
            {var subQ0=sQuery(id+"F0.wireOp",EDGE,"E3");Q2=makeQuery(id+"F11.boolean.opBoolean","INTERSECT",EDGE,{"derivedFrom":[makeQuery(id+"F3.opFillet","BLEND_FACE",FACE,{"disambiguationData":[OSD([subQ0]),TDD([makeQuery(id+"F1.opExtrude","CAP_EDGE",EDGE,{"disambiguationData":[OSD([subQ0]),TDD([makeQuery(id+"F0.imprint","IMPRINT",EDGE,{"disambiguationData":[TD([[makeQuery(id+"F0.imprint","INTERSECT",VERTEX,{"derivedFrom":[subQ0,sQuery(id+"F0.wireOp",EDGE,"E11")]}),-1.0]])],"derivedFrom":subQ0})])],"isStart":false})])]}),makeQuery(id+"F11.opExtrude","CAP_FACE",FACE,{"disambiguationData":[OSD([sQuery(id+"F10.wireOp",EDGE,"E31"),sQuery(id+"F10.wireOp",EDGE,"E33"),sQuery(id+"F10.wireOp",EDGE,"E34"),sQuery(id+"F10.wireOp",EDGE,"E35"),sQuery(id+"F10.wireOp",EDGE,"E36"),sQuery(id+"F10.wireOp",EDGE,"E37"),sQuery(id+"F10.wireOp",EDGE,"E38")])],"isStart":false})]});}
            fillet(context, id + "F12", {"entities" : qUnion([Q0, Q1, Q2]), "radius" : 1 * mm, "tangentPropagation" : true, "allowEdgeOverflow" : false});
        }
    });
